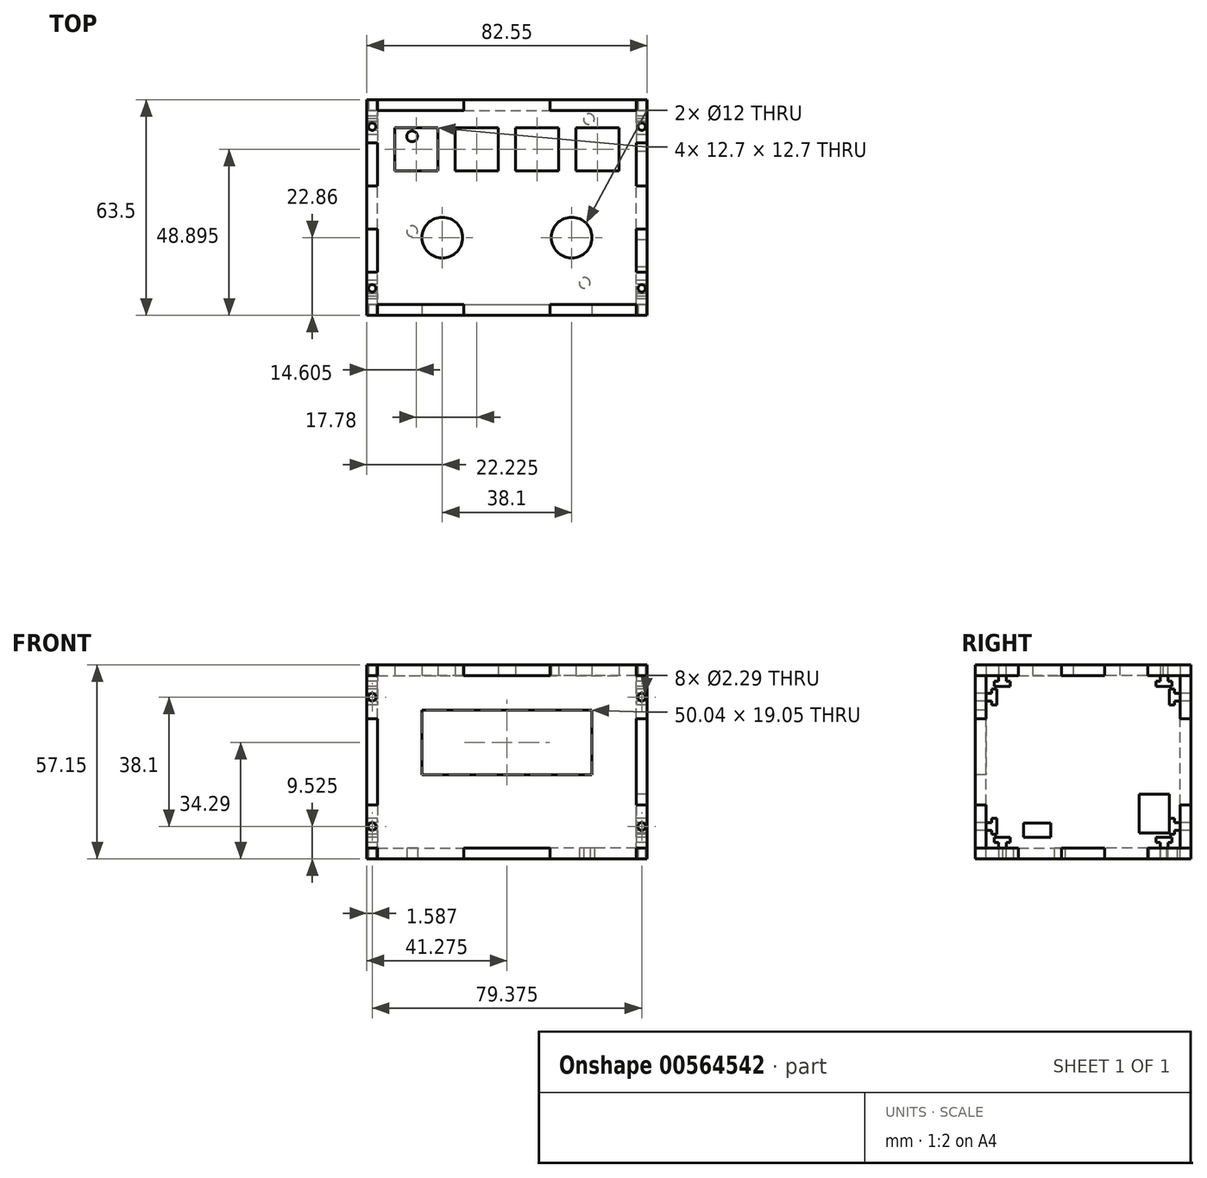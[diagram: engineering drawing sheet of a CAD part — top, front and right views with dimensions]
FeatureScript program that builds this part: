
annotation { "Feature Type Name" : "Feature", "Feature Type Description" : "" }
export const myFeature = defineFeature(function(context is Context, id is Id, definition is map)
    precondition{}
    {
        {
            var Q0;
            Q0=qCreatedBy(makeId("Top.planeOp"),FACE);
            var sketch = newSketch(context, id + "F0", { "sketchPlane" : qUnion([Q0])});
            skLineSegment(sketch, "E0.bottom", {"start": v(0, 0) * mm, "end": v(3.18, 0) * mm});
            skLineSegment(sketch, "E0.top", {"start": v(0, 63.5) * mm, "end": v(3.18, 63.5) * mm});
            skLineSegment(sketch, "E0.left", {"start": v(0, 0) * mm, "end": v(0, 12.7) * mm});
            skLineSegment(sketch, "E0.right", {"start": v(82.55, 0) * mm, "end": v(82.55, 12.7) * mm});
            skLineSegment(sketch, "E1", {"start": v(0, 12.7) * mm, "end": v(3.17, 12.7) * mm});
            skLineSegment(sketch, "E2", {"start": v(3.17, 12.7) * mm, "end": v(3.17, 25.4) * mm});
            skLineSegment(sketch, "E3", {"start": v(3.17, 25.4) * mm, "end": v(0, 25.4) * mm});
            skLineSegment(sketch, "E4.MirrorCS", {"start": v(0, 50.8) * mm, "end": v(3.17, 50.8) * mm});
            skLineSegment(sketch, "E5.MirrorCS", {"start": v(3.17, 38.1) * mm, "end": v(0, 38.1) * mm});
            skLineSegment(sketch, "E6.MirrorCS", {"start": v(3.17, 50.8) * mm, "end": v(3.17, 38.1) * mm});
            skLineSegment(sketch, "E7.MirrorCS", {"start": v(0, 63.5) * mm, "end": v(0, 50.8) * mm});
            skLineSegment(sketch, "E8.MirrorCS", {"start": v(82.55, 12.7) * mm, "end": v(79.37, 12.7) * mm});
            skLineSegment(sketch, "E9.MirrorCS", {"start": v(82.55, 50.8) * mm, "end": v(79.37, 50.8) * mm});
            skLineSegment(sketch, "E10.MirrorCS", {"start": v(79.37, 38.1) * mm, "end": v(82.55, 38.1) * mm});
            skLineSegment(sketch, "E11.MirrorCS", {"start": v(79.37, 25.4) * mm, "end": v(82.55, 25.4) * mm});
            skLineSegment(sketch, "E12.MirrorCS", {"start": v(79.37, 12.7) * mm, "end": v(79.37, 25.4) * mm});
            skLineSegment(sketch, "E13.MirrorCS", {"start": v(79.37, 50.8) * mm, "end": v(79.37, 38.1) * mm});
            skLineSegment(sketch, "E14.trimOffspring", {"start": v(0, 50.8) * mm, "end": v(0, 63.5) * mm});
            skLineSegment(sketch, "E15.trimOffspring", {"start": v(0, 25.4) * mm, "end": v(0, 38.1) * mm});
            skPoint(sketch, "E16.end.orphan", {"position": v(2.08, 31.75) * mm});
            skPoint(sketch, "E16.start.orphan", {"position": v(0, 31.75) * mm});
            skLineSegment(sketch, "E17.trimOffspring", {"start": v(0, 38.1) * mm, "end": v(0, 25.4) * mm});
            skLineSegment(sketch, "E18.trimOffspring", {"start": v(0, 12.7) * mm, "end": v(0, 0) * mm});
            skLineSegment(sketch, "E19.trimOffspring", {"start": v(82.55, 50.8) * mm, "end": v(82.55, 63.5) * mm});
            skLineSegment(sketch, "E20.trimOffspring", {"start": v(82.55, 25.4) * mm, "end": v(82.55, 38.1) * mm});
            skPoint(sketch, "E21.MirrorCS.end.orphan", {"position": v(80.47, 31.75) * mm});
            skPoint(sketch, "E21.MirrorCS.start.orphan", {"position": v(82.55, 31.75) * mm});
            skLineSegment(sketch, "E22", {"start": v(3.18, 0) * mm, "end": v(3.18, 3.17) * mm});
            skLineSegment(sketch, "E23", {"start": v(3.18, 3.17) * mm, "end": v(28.58, 3.17) * mm});
            skLineSegment(sketch, "E24", {"start": v(28.58, 3.17) * mm, "end": v(28.58, 0) * mm});
            skLineSegment(sketch, "E25.MirrorCS", {"start": v(79.37, 0) * mm, "end": v(79.37, 3.17) * mm});
            skLineSegment(sketch, "E26.MirrorCS", {"start": v(79.37, 0) * mm, "end": v(79.37, 0) * mm});
            skLineSegment(sketch, "E27.MirrorCS", {"start": v(53.97, 3.17) * mm, "end": v(53.97, 0) * mm});
            skLineSegment(sketch, "E28.MirrorCS", {"start": v(53.97, 0) * mm, "end": v(28.58, 0) * mm});
            skLineSegment(sketch, "E29.MirrorCS", {"start": v(79.37, 3.17) * mm, "end": v(53.97, 3.17) * mm});
            skLineSegment(sketch, "E30.MirrorCS", {"start": v(79.37, 63.5) * mm, "end": v(79.37, 63.5) * mm});
            skLineSegment(sketch, "E31.MirrorCS", {"start": v(3.18, 63.5) * mm, "end": v(3.18, 60.33) * mm});
            skLineSegment(sketch, "E32.MirrorCS", {"start": v(79.37, 63.5) * mm, "end": v(79.37, 60.33) * mm});
            skLineSegment(sketch, "E33.MirrorCS", {"start": v(53.97, 60.33) * mm, "end": v(53.97, 63.5) * mm});
            skLineSegment(sketch, "E34.MirrorCS", {"start": v(28.58, 60.33) * mm, "end": v(28.58, 63.5) * mm});
            skLineSegment(sketch, "E35.MirrorCS", {"start": v(79.37, 60.33) * mm, "end": v(53.97, 60.33) * mm});
            skLineSegment(sketch, "E36.MirrorCS", {"start": v(3.18, 60.33) * mm, "end": v(28.58, 60.33) * mm});
            skLineSegment(sketch, "E37.trimOffspring", {"start": v(28.58, 63.5) * mm, "end": v(53.97, 63.5) * mm});
            skLineSegment(sketch, "E38.trimOffspring", {"start": v(79.37, 63.5) * mm, "end": v(82.55, 63.5) * mm});
            skPoint(sketch, "E39.start.orphan", {"position": v(41.27, 63.5) * mm});
            skLineSegment(sketch, "E40.trimOffspring", {"start": v(3.17, 0) * mm, "end": v(0, 0) * mm});
            skLineSegment(sketch, "E41.trimOffspring", {"start": v(79.37, 0) * mm, "end": v(82.55, 0) * mm});
            skLineSegment(sketch, "E42.trimOffspring", {"start": v(28.58, 0) * mm, "end": v(53.97, 0) * mm});
            skLineSegment(sketch, "E43", {"start": v(79.37, 60.33) * mm, "end": v(65.4, 60.33) * mm});
            skLineSegment(sketch, "E44", {"start": v(79.37, 3.17) * mm, "end": v(64.13, 3.17) * mm});
            skCircle(sketch, "E45", {"center": v(65.4, 57.78) * mm, "radius": 1.59 * mm});
            skCircle(sketch, "E46", {"center": v(64.13, 9.52) * mm, "radius": 1.59 * mm});
            skCircle(sketch, "E47", {"center": v(13.33, 52.7) * mm, "radius": 1.59 * mm});
            skCircle(sketch, "E48", {"center": v(13.33, 24.76) * mm, "radius": 1.59 * mm});
            skLineSegment(sketch, "E49.trimOffspring", {"start": v(28.58, 60.33) * mm, "end": v(13.33, 60.33) * mm});
            skLineSegment(sketch, "E50.trimOffspring", {"start": v(28.58, 60.33) * mm, "end": v(14.3, 60.33) * mm});
            skPoint(sketch, "E51.start.orphan", {"position": v(64.13, 57.78) * mm});
            skLineSegment(sketch, "E52", {"start": v(82.55, 0) * mm, "end": v(82.55, 7.94) * mm});
            skLineSegment(sketch, "E53", {"start": v(82.55, 0) * mm, "end": v(80.96, 0) * mm});
            skCircle(sketch, "E54", {"center": v(1.59, 7.94) * mm, "radius": 1.09 * mm});
            skPoint(sketch, "E55.endSnap0", {"position": v(41.28, 63.5) * mm});
            skCircle(sketch, "E56.MirrorC", {"center": v(1.59, 55.56) * mm, "radius": 1.09 * mm});
            skCircle(sketch, "E57.MirrorC", {"center": v(80.96, 55.56) * mm, "radius": 1.09 * mm});
            skCircle(sketch, "E58.MirrorC", {"center": v(80.96, 7.94) * mm, "radius": 1.09 * mm});
            skPoint(sketch, "E59.MirrorCS.start.orphan", {"position": v(0, 55.56) * mm});
            skPoint(sketch, "E60.start.orphan", {"position": v(0, 7.94) * mm});
            skPoint(sketch, "E55.end.orphan", {"position": v(41.28, 60.47) * mm});
            skPoint(sketch, "E55.start.orphan", {"position": v(41.28, 63.5) * mm});
            skSolve(sketch);
        }
        {
            var Q0;
            Q0=makeQuery(id+"F0.imprint","IMPRINT",FACE,{"disambiguationData":[TD([[makeQuery(id+"F0.imprint","IMPRINT",EDGE,{"derivedFrom":sQuery(id+"F0.wireOp",EDGE,"E0.top")}),-1.0]])]});
            extrude(context, id + "F1", {"entities" : qUnion([Q0]), "depth" : 3.17 * mm, "offsetDistance" : 25.4 * mm});
        }
        {
            var Q0;
            Q0=qCreatedBy(makeId("Right.planeOp"),FACE);
            var sketch = newSketch(context, id + "F2", { "sketchPlane" : qUnion([Q0])});
            skLineSegment(sketch, "E61.top", {"start": v(12.7, 57.15) * mm, "end": v(25.4, 57.15) * mm});
            skLineSegment(sketch, "E62", {"start": v(3.18, 3.18) * mm, "end": v(6.8, 3.18) * mm});
            skLineSegment(sketch, "E63", {"start": v(12.7, 3.18) * mm, "end": v(12.7, 0) * mm});
            skLineSegment(sketch, "E64", {"start": v(12.7, 0) * mm, "end": v(25.4, 0) * mm});
            skLineSegment(sketch, "E65", {"start": v(25.4, 0) * mm, "end": v(25.4, 3.18) * mm});
            skLineSegment(sketch, "E66", {"start": v(25.4, 3.18) * mm, "end": v(38.1, 3.18) * mm});
            skLineSegment(sketch, "E67.MirrorCS", {"start": v(38.1, 0) * mm, "end": v(38.1, 3.18) * mm});
            skLineSegment(sketch, "E68.MirrorCS", {"start": v(50.8, 3.18) * mm, "end": v(50.8, 0) * mm});
            skLineSegment(sketch, "E69.MirrorCS", {"start": v(50.8, 0) * mm, "end": v(38.1, 0) * mm});
            skLineSegment(sketch, "E70.MirrorCS", {"start": v(38.1, 3.18) * mm, "end": v(25.4, 3.18) * mm});
            skLineSegment(sketch, "E71.MirrorCS", {"start": v(50.8, 53.98) * mm, "end": v(50.8, 57.15) * mm});
            skLineSegment(sketch, "E72.MirrorCS", {"start": v(38.1, 57.15) * mm, "end": v(38.1, 53.98) * mm});
            skLineSegment(sketch, "E73.MirrorCS", {"start": v(12.7, 53.98) * mm, "end": v(12.7, 57.15) * mm});
            skLineSegment(sketch, "E74.MirrorCS", {"start": v(25.4, 57.15) * mm, "end": v(25.4, 53.98) * mm});
            skLineSegment(sketch, "E75.MirrorCS", {"start": v(25.4, 53.98) * mm, "end": v(38.1, 53.98) * mm});
            skLineSegment(sketch, "E76.MirrorCS", {"start": v(38.1, 53.98) * mm, "end": v(25.4, 53.98) * mm});
            skLineSegment(sketch, "E77.MirrorCS", {"start": v(50.8, 57.15) * mm, "end": v(38.1, 57.15) * mm});
            skLineSegment(sketch, "E78.MirrorCS", {"start": v(60.32, 53.98) * mm, "end": v(56.7, 53.98) * mm});
            skLineSegment(sketch, "E79.MirrorCS", {"start": v(3.18, 53.98) * mm, "end": v(6.8, 53.98) * mm});
            skLineSegment(sketch, "E80.trimOffspring", {"start": v(38.1, 57.15) * mm, "end": v(50.8, 57.15) * mm});
            skPoint(sketch, "E81.orphan", {"position": v(31.75, 57.15) * mm});
            skPoint(sketch, "E82.MirrorCS.start.orphan", {"position": v(63.5, 57.15) * mm});
            skLineSegment(sketch, "E83.trimOffspring", {"start": v(38.1, 0) * mm, "end": v(50.8, 0) * mm});
            skPoint(sketch, "E84.MirrorCS.start.orphan", {"position": v(63.5, 0) * mm});
            skPoint(sketch, "E85.orphan", {"position": v(0, 57.15) * mm});
            skLineSegment(sketch, "E86", {"start": v(0, 15.87) * mm, "end": v(3.18, 15.87) * mm});
            skLineSegment(sketch, "E87", {"start": v(3.18, 15.87) * mm, "end": v(3.18, 10.67) * mm});
            skLineSegment(sketch, "E88.trimOffspring", {"start": v(0, 15.87) * mm, "end": v(0, 41.28) * mm});
            skLineSegment(sketch, "E89.MirrorCS", {"start": v(3.18, 41.28) * mm, "end": v(3.18, 46.48) * mm});
            skLineSegment(sketch, "E90.MirrorCS", {"start": v(0, 41.28) * mm, "end": v(0, 15.87) * mm});
            skLineSegment(sketch, "E91.MirrorCS", {"start": v(0, 41.28) * mm, "end": v(3.18, 41.28) * mm});
            skLineSegment(sketch, "E92.MirrorCS", {"start": v(63.5, 41.28) * mm, "end": v(60.32, 41.28) * mm});
            skLineSegment(sketch, "E93.MirrorCS", {"start": v(63.5, 15.87) * mm, "end": v(60.32, 15.87) * mm});
            skLineSegment(sketch, "E94.MirrorCS", {"start": v(60.32, 41.28) * mm, "end": v(60.32, 46.48) * mm});
            skLineSegment(sketch, "E95.MirrorCS", {"start": v(63.5, 15.87) * mm, "end": v(63.5, 41.28) * mm});
            skLineSegment(sketch, "E96.MirrorCS", {"start": v(60.32, 15.87) * mm, "end": v(60.32, 10.67) * mm});
            skLineSegment(sketch, "E97.MirrorCS", {"start": v(63.5, 41.28) * mm, "end": v(63.5, 15.87) * mm});
            skPoint(sketch, "E98.MirrorCS.end.orphan", {"position": v(58.61, 28.58) * mm});
            skPoint(sketch, "E98.MirrorCS.start.orphan", {"position": v(63.5, 28.58) * mm});
            skPoint(sketch, "E99.orphan", {"position": v(63.5, 3.17) * mm});
            skPoint(sketch, "E100.orphan", {"position": v(0, 3.17) * mm});
            skPoint(sketch, "E101.end.orphan", {"position": v(4.89, 28.58) * mm});
            skPoint(sketch, "E101.start.orphan", {"position": v(0, 28.58) * mm});
            skPoint(sketch, "E61.left.start.orphan", {"position": v(0, 0) * mm});
            skLineSegment(sketch, "E102.top", {"start": v(56.7, 6.35) * mm, "end": v(54.42, 6.35) * mm});
            skLineSegment(sketch, "E102.left", {"start": v(56.7, 3.18) * mm, "end": v(56.7, 4.83) * mm});
            skLineSegment(sketch, "E102.right", {"start": v(54.42, 3.18) * mm, "end": v(54.42, 4.83) * mm});
            skPoint(sketch, "E103.end.orphan", {"position": v(54.42, 3.18) * mm});
            skLineSegment(sketch, "E104.trimOffspring", {"start": v(54.42, 3.18) * mm, "end": v(50.8, 3.18) * mm});
            skPoint(sketch, "E105.start.orphan", {"position": v(55.56, 3.18) * mm});
            skLineSegment(sketch, "E106", {"start": v(56.7, 3.18) * mm, "end": v(60.32, 3.18) * mm});
            skLineSegment(sketch, "E107.bottom", {"start": v(57.91, 6.35) * mm, "end": v(53.21, 6.35) * mm});
            skLineSegment(sketch, "E107.top", {"start": v(57.91, 4.83) * mm, "end": v(56.7, 4.83) * mm});
            skLineSegment(sketch, "E107.left", {"start": v(57.91, 6.35) * mm, "end": v(57.91, 4.83) * mm});
            skLineSegment(sketch, "E107.right", {"start": v(53.21, 6.35) * mm, "end": v(53.21, 4.83) * mm});
            skPoint(sketch, "E107.middle", {"position": v(55.56, 5.59) * mm});
            skLineSegment(sketch, "E108.trimOffspring", {"start": v(54.42, 4.83) * mm, "end": v(53.21, 4.83) * mm});
            skPoint(sketch, "E109.start.orphan", {"position": v(55.56, 6.35) * mm});
            skLineSegment(sketch, "E110.MirrorCS", {"start": v(54.42, 52.32) * mm, "end": v(53.21, 52.32) * mm});
            skLineSegment(sketch, "E111.MirrorCS", {"start": v(57.91, 52.32) * mm, "end": v(56.7, 52.32) * mm});
            skLineSegment(sketch, "E112.MirrorCS", {"start": v(56.7, 53.98) * mm, "end": v(56.7, 52.32) * mm});
            skLineSegment(sketch, "E113.MirrorCS", {"start": v(54.42, 53.98) * mm, "end": v(54.42, 52.32) * mm});
            skLineSegment(sketch, "E114.MirrorCS", {"start": v(56.7, 50.8) * mm, "end": v(54.42, 50.8) * mm});
            skLineSegment(sketch, "E115.MirrorCS", {"start": v(53.21, 50.8) * mm, "end": v(53.21, 52.32) * mm});
            skPoint(sketch, "E116.MirrorP", {"position": v(54.42, 53.98) * mm});
            skPoint(sketch, "E117.MirrorP", {"position": v(55.56, 50.8) * mm});
            skLineSegment(sketch, "E118.MirrorCS", {"start": v(57.91, 50.8) * mm, "end": v(53.21, 50.8) * mm});
            skLineSegment(sketch, "E119.MirrorCS", {"start": v(57.91, 50.8) * mm, "end": v(57.91, 52.32) * mm});
            skPoint(sketch, "E120.MirrorP", {"position": v(55.56, 53.98) * mm});
            skPoint(sketch, "E121.MirrorP", {"position": v(55.56, 51.56) * mm});
            skLineSegment(sketch, "E122.MirrorCS", {"start": v(6.8, 6.35) * mm, "end": v(9.08, 6.35) * mm});
            skLineSegment(sketch, "E123.MirrorCS", {"start": v(9.08, 4.83) * mm, "end": v(10.29, 4.83) * mm});
            skLineSegment(sketch, "E124.MirrorCS", {"start": v(9.08, 3.18) * mm, "end": v(9.08, 4.83) * mm});
            skLineSegment(sketch, "E125.MirrorCS", {"start": v(6.8, 3.18) * mm, "end": v(6.8, 4.83) * mm});
            skLineSegment(sketch, "E126.MirrorCS", {"start": v(5.59, 4.83) * mm, "end": v(6.8, 4.83) * mm});
            skLineSegment(sketch, "E127.MirrorCS", {"start": v(6.8, 3.18) * mm, "end": v(3.17, 3.18) * mm});
            skPoint(sketch, "E128.MirrorP", {"position": v(7.94, 6.35) * mm});
            skLineSegment(sketch, "E129.MirrorCS", {"start": v(9.08, 3.18) * mm, "end": v(12.7, 3.18) * mm});
            skLineSegment(sketch, "E130.MirrorCS", {"start": v(5.59, 6.35) * mm, "end": v(10.29, 6.35) * mm});
            skPoint(sketch, "E131.MirrorP", {"position": v(9.08, 3.18) * mm});
            skPoint(sketch, "E132.MirrorP", {"position": v(7.94, 5.59) * mm});
            skLineSegment(sketch, "E133.MirrorCS", {"start": v(5.59, 6.35) * mm, "end": v(5.59, 4.83) * mm});
            skLineSegment(sketch, "E134.MirrorCS", {"start": v(10.29, 6.35) * mm, "end": v(10.29, 4.83) * mm});
            skPoint(sketch, "E135.MirrorP", {"position": v(7.94, 3.18) * mm});
            skLineSegment(sketch, "E136.MirrorCS", {"start": v(6.8, 50.8) * mm, "end": v(9.08, 50.8) * mm});
            skLineSegment(sketch, "E137.MirrorCS", {"start": v(10.29, 50.8) * mm, "end": v(10.29, 52.32) * mm});
            skLineSegment(sketch, "E138.MirrorCS", {"start": v(9.08, 52.32) * mm, "end": v(10.29, 52.32) * mm});
            skLineSegment(sketch, "E139.MirrorCS", {"start": v(6.8, 53.98) * mm, "end": v(6.8, 52.32) * mm});
            skPoint(sketch, "E140.MirrorP", {"position": v(7.94, 51.56) * mm});
            skLineSegment(sketch, "E141.MirrorCS", {"start": v(5.59, 50.8) * mm, "end": v(10.29, 50.8) * mm});
            skLineSegment(sketch, "E142.MirrorCS", {"start": v(5.59, 50.8) * mm, "end": v(5.59, 52.32) * mm});
            skLineSegment(sketch, "E143.MirrorCS", {"start": v(5.59, 52.32) * mm, "end": v(6.8, 52.32) * mm});
            skPoint(sketch, "E144.MirrorP", {"position": v(9.08, 53.98) * mm});
            skPoint(sketch, "E145.MirrorP", {"position": v(7.94, 50.8) * mm});
            skPoint(sketch, "E146.MirrorP", {"position": v(7.94, 53.98) * mm});
            skLineSegment(sketch, "E147.MirrorCS", {"start": v(9.08, 53.98) * mm, "end": v(9.08, 52.32) * mm});
            skLineSegment(sketch, "E148.trimOffspring", {"start": v(54.42, 53.98) * mm, "end": v(50.8, 53.98) * mm});
            skLineSegment(sketch, "E149.trimOffspring", {"start": v(9.08, 53.98) * mm, "end": v(12.7, 53.98) * mm});
            skPoint(sketch, "E150.MirrorCS.start.orphan", {"position": v(3.17, 53.98) * mm});
            skLineSegment(sketch, "E151.bottom", {"start": v(60.32, 10.67) * mm, "end": v(58.67, 10.67) * mm});
            skLineSegment(sketch, "E151.top", {"start": v(60.32, 8.38) * mm, "end": v(58.67, 8.38) * mm});
            skLineSegment(sketch, "E151.right", {"start": v(57.15, 10.67) * mm, "end": v(57.15, 8.38) * mm});
            skLineSegment(sketch, "E152.bottom", {"start": v(57.15, 7.18) * mm, "end": v(58.67, 7.18) * mm});
            skLineSegment(sketch, "E152.top", {"start": v(57.15, 11.87) * mm, "end": v(58.67, 11.87) * mm});
            skLineSegment(sketch, "E152.left", {"start": v(57.15, 7.18) * mm, "end": v(57.15, 11.87) * mm});
            skLineSegment(sketch, "E152.right", {"start": v(58.67, 7.18) * mm, "end": v(58.67, 8.38) * mm});
            skPoint(sketch, "E152.middle", {"position": v(57.91, 9.52) * mm});
            skLineSegment(sketch, "E153.trimOffspring", {"start": v(58.67, 10.67) * mm, "end": v(58.67, 11.87) * mm});
            skPoint(sketch, "E154.start.orphan", {"position": v(57.15, 9.53) * mm});
            skLineSegment(sketch, "E155.trimOffspring", {"start": v(60.32, 8.38) * mm, "end": v(60.32, 3.18) * mm});
            skPoint(sketch, "E156.orphan", {"position": v(60.32, 8.38) * mm});
            skPoint(sketch, "E151.left.end.orphan", {"position": v(60.32, 9.52) * mm});
            skPoint(sketch, "E157.MirrorP", {"position": v(57.91, 47.63) * mm});
            skPoint(sketch, "E158.MirrorP", {"position": v(57.15, 47.63) * mm});
            skLineSegment(sketch, "E159.MirrorCS", {"start": v(57.15, 46.48) * mm, "end": v(57.15, 48.77) * mm});
            skLineSegment(sketch, "E160.MirrorCS", {"start": v(57.15, 45.28) * mm, "end": v(58.67, 45.28) * mm});
            skLineSegment(sketch, "E161.MirrorCS", {"start": v(57.15, 49.97) * mm, "end": v(57.15, 45.28) * mm});
            skLineSegment(sketch, "E162.MirrorCS", {"start": v(60.32, 48.77) * mm, "end": v(58.67, 48.77) * mm});
            skLineSegment(sketch, "E163.MirrorCS", {"start": v(57.15, 49.97) * mm, "end": v(58.67, 49.97) * mm});
            skLineSegment(sketch, "E164.MirrorCS", {"start": v(60.32, 46.48) * mm, "end": v(58.67, 46.48) * mm});
            skLineSegment(sketch, "E165.MirrorCS", {"start": v(58.67, 49.97) * mm, "end": v(58.67, 48.77) * mm});
            skLineSegment(sketch, "E166.MirrorCS", {"start": v(58.67, 46.48) * mm, "end": v(58.67, 45.28) * mm});
            skLineSegment(sketch, "E167.MirrorCS", {"start": v(6.35, 46.48) * mm, "end": v(6.35, 48.77) * mm});
            skLineSegment(sketch, "E168.MirrorCS", {"start": v(3.17, 41.28) * mm, "end": v(3.17, 46.48) * mm});
            skLineSegment(sketch, "E169.MirrorCS", {"start": v(6.35, 49.97) * mm, "end": v(4.83, 49.97) * mm});
            skLineSegment(sketch, "E170.MirrorCS", {"start": v(6.35, 49.97) * mm, "end": v(6.35, 45.28) * mm});
            skPoint(sketch, "E171.MirrorP", {"position": v(5.59, 47.63) * mm});
            skLineSegment(sketch, "E172.MirrorCS", {"start": v(4.83, 46.48) * mm, "end": v(4.83, 45.28) * mm});
            skLineSegment(sketch, "E173.MirrorCS", {"start": v(3.17, 46.48) * mm, "end": v(4.83, 46.48) * mm});
            skLineSegment(sketch, "E174.MirrorCS", {"start": v(4.83, 49.97) * mm, "end": v(4.83, 48.77) * mm});
            skLineSegment(sketch, "E175.MirrorCS", {"start": v(3.17, 48.77) * mm, "end": v(4.83, 48.77) * mm});
            skLineSegment(sketch, "E176.MirrorCS", {"start": v(6.35, 45.28) * mm, "end": v(4.83, 45.28) * mm});
            skPoint(sketch, "E177.MirrorP", {"position": v(6.35, 47.63) * mm});
            skPoint(sketch, "E178.MirrorP", {"position": v(5.59, 9.52) * mm});
            skPoint(sketch, "E179.MirrorP", {"position": v(6.35, 9.52) * mm});
            skLineSegment(sketch, "E180.MirrorCS", {"start": v(6.35, 10.67) * mm, "end": v(6.35, 8.38) * mm});
            skLineSegment(sketch, "E181.MirrorCS", {"start": v(3.17, 8.38) * mm, "end": v(4.83, 8.38) * mm});
            skLineSegment(sketch, "E182.MirrorCS", {"start": v(6.35, 7.18) * mm, "end": v(6.35, 11.87) * mm});
            skLineSegment(sketch, "E183.MirrorCS", {"start": v(4.83, 10.67) * mm, "end": v(4.83, 11.87) * mm});
            skPoint(sketch, "E184.MirrorP", {"position": v(3.17, 9.52) * mm});
            skLineSegment(sketch, "E185.MirrorCS", {"start": v(3.17, 8.38) * mm, "end": v(3.17, 3.18) * mm});
            skLineSegment(sketch, "E186.MirrorCS", {"start": v(3.17, 10.67) * mm, "end": v(4.83, 10.67) * mm});
            skLineSegment(sketch, "E187.MirrorCS", {"start": v(4.83, 7.18) * mm, "end": v(4.83, 8.38) * mm});
            skLineSegment(sketch, "E188.MirrorCS", {"start": v(3.17, 15.87) * mm, "end": v(3.17, 10.67) * mm});
            skLineSegment(sketch, "E189.MirrorCS", {"start": v(6.35, 7.18) * mm, "end": v(4.83, 7.18) * mm});
            skLineSegment(sketch, "E190.MirrorCS", {"start": v(6.35, 11.87) * mm, "end": v(4.83, 11.87) * mm});
            skPoint(sketch, "E191.MirrorP", {"position": v(3.17, 8.38) * mm});
            skLineSegment(sketch, "E192.trimOffspring", {"start": v(60.32, 48.77) * mm, "end": v(60.32, 53.98) * mm});
            skLineSegment(sketch, "E193.trimOffspring", {"start": v(3.17, 48.77) * mm, "end": v(3.17, 53.98) * mm});
            skLineSegment(sketch, "E194.trimOffspring", {"start": v(3.18, 8.38) * mm, "end": v(3.18, 3.18) * mm});
            skLineSegment(sketch, "E195.trimOffspring", {"start": v(3.18, 48.77) * mm, "end": v(3.18, 53.98) * mm});
            skPoint(sketch, "E196.start.orphan", {"position": v(31.75, 3.18) * mm});
            skSolve(sketch);
        }
        {
            var Q0;
            Q0 = qSketchRegion(id + "F2", true);
            extrude(context, id + "F3", {"entities" : qUnion([Q0]), "depth" : 3.17 * mm, "offsetDistance" : 25.4 * mm});
        }
        {
            var Q0;
            Q0=qCreatedBy(makeId("Front.planeOp"),FACE);
            var sketch = newSketch(context, id + "F4", { "sketchPlane" : qUnion([Q0])});
            skLineSegment(sketch, "E197.bottom", {"start": v(3.17, 0) * mm, "end": v(28.58, 0) * mm});
            skLineSegment(sketch, "E197.top", {"start": v(3.17, 57.15) * mm, "end": v(28.58, 57.15) * mm});
            skLineSegment(sketch, "E198.top", {"start": v(0, 3.18) * mm, "end": v(3.17, 3.18) * mm});
            skLineSegment(sketch, "E198.right", {"start": v(3.18, 0) * mm, "end": v(3.17, 3.18) * mm});
            skLineSegment(sketch, "E199", {"start": v(3.18, 0) * mm, "end": v(28.58, 0) * mm});
            skLineSegment(sketch, "E200.top", {"start": v(28.58, 3.18) * mm, "end": v(53.98, 3.18) * mm});
            skLineSegment(sketch, "E200.left", {"start": v(28.58, 0) * mm, "end": v(28.58, 3.18) * mm});
            skLineSegment(sketch, "E200.right", {"start": v(53.98, 0) * mm, "end": v(53.98, 3.18) * mm});
            skPoint(sketch, "E201.endSnap0", {"position": v(41.28, 3.18) * mm});
            skLineSegment(sketch, "E202.MirrorCS", {"start": v(82.55, 3.18) * mm, "end": v(79.38, 3.17) * mm});
            skLineSegment(sketch, "E203.MirrorCS", {"start": v(79.38, 0) * mm, "end": v(79.38, 3.18) * mm});
            skLineSegment(sketch, "E204.MirrorCS", {"start": v(82.55, 53.98) * mm, "end": v(79.38, 53.98) * mm});
            skLineSegment(sketch, "E205.MirrorCS", {"start": v(53.98, 57.15) * mm, "end": v(53.98, 53.98) * mm});
            skLineSegment(sketch, "E206.MirrorCS", {"start": v(28.58, 57.15) * mm, "end": v(28.58, 53.98) * mm});
            skLineSegment(sketch, "E207.MirrorCS", {"start": v(0, 53.98) * mm, "end": v(3.17, 53.98) * mm});
            skLineSegment(sketch, "E208.MirrorCS", {"start": v(3.18, 57.15) * mm, "end": v(3.17, 53.98) * mm});
            skLineSegment(sketch, "E209.MirrorCS", {"start": v(79.38, 57.15) * mm, "end": v(79.38, 53.98) * mm});
            skLineSegment(sketch, "E210.MirrorCS", {"start": v(28.58, 53.98) * mm, "end": v(53.98, 53.98) * mm});
            skLineSegment(sketch, "E211.MirrorCS", {"start": v(3.18, 57.15) * mm, "end": v(28.58, 57.15) * mm});
            skPoint(sketch, "E212.MirrorP", {"position": v(41.28, 53.98) * mm});
            skPoint(sketch, "E213.orphan", {"position": v(0, 57.15) * mm});
            skPoint(sketch, "E214.orphan", {"position": v(82.55, 57.15) * mm});
            skPoint(sketch, "E215.start.orphan", {"position": v(0, 28.58) * mm});
            skPoint(sketch, "E216.MirrorCS.start.orphan", {"position": v(82.55, 0) * mm});
            skLineSegment(sketch, "E217.trimOffspring", {"start": v(53.98, 57.15) * mm, "end": v(79.38, 57.15) * mm});
            skLineSegment(sketch, "E218", {"start": v(53.98, 0) * mm, "end": v(79.38, 0) * mm});
            skLineSegment(sketch, "E219", {"start": v(0, 3.18) * mm, "end": v(0, 15.88) * mm});
            skLineSegment(sketch, "E220.bottom", {"start": v(0, 15.88) * mm, "end": v(3.18, 15.88) * mm});
            skLineSegment(sketch, "E220.top", {"start": v(0, 41.28) * mm, "end": v(3.17, 41.28) * mm});
            skLineSegment(sketch, "E220.right", {"start": v(3.18, 15.88) * mm, "end": v(3.17, 41.28) * mm});
            skLineSegment(sketch, "E221.trimOffspring", {"start": v(0, 41.28) * mm, "end": v(0, 53.98) * mm});
            skLineSegment(sketch, "E222.MirrorCS", {"start": v(82.55, 41.28) * mm, "end": v(82.55, 53.98) * mm});
            skLineSegment(sketch, "E223.MirrorCS", {"start": v(79.38, 57.15) * mm, "end": v(53.98, 57.15) * mm});
            skLineSegment(sketch, "E224.MirrorCS", {"start": v(82.55, 3.18) * mm, "end": v(79.38, 3.18) * mm});
            skLineSegment(sketch, "E225.MirrorCS", {"start": v(82.55, 15.88) * mm, "end": v(79.38, 15.88) * mm});
            skLineSegment(sketch, "E226.MirrorCS", {"start": v(82.55, 41.28) * mm, "end": v(79.38, 41.28) * mm});
            skLineSegment(sketch, "E227.MirrorCS", {"start": v(79.38, 0) * mm, "end": v(53.98, 0) * mm});
            skLineSegment(sketch, "E228.MirrorCS", {"start": v(82.55, 3.18) * mm, "end": v(82.55, 15.88) * mm});
            skPoint(sketch, "E229.MirrorP", {"position": v(82.55, 28.58) * mm});
            skLineSegment(sketch, "E230.MirrorCS", {"start": v(79.38, 15.88) * mm, "end": v(79.38, 41.28) * mm});
            skPoint(sketch, "E231.orphan", {"position": v(28.58, 0) * mm});
            skPoint(sketch, "E201.end.orphan", {"position": v(41.28, 6.6) * mm});
            skPoint(sketch, "E201.start.orphan", {"position": v(41.28, 3.18) * mm});
            skPoint(sketch, "E232.orphan", {"position": v(0, 0) * mm});
            skLineSegment(sketch, "E233.bottom", {"start": v(16.26, 43.82) * mm, "end": v(66.3, 43.82) * mm});
            skLineSegment(sketch, "E233.top", {"start": v(16.26, 24.77) * mm, "end": v(66.3, 24.77) * mm});
            skLineSegment(sketch, "E233.left", {"start": v(16.26, 43.82) * mm, "end": v(16.26, 24.77) * mm});
            skLineSegment(sketch, "E233.right", {"start": v(66.3, 43.82) * mm, "end": v(66.3, 24.77) * mm});
            skPoint(sketch, "E233.middle", {"position": v(41.28, 34.3) * mm});
            skLineSegment(sketch, "E234", {"start": v(0, 0) * mm, "end": v(0, 9.53) * mm});
            skCircle(sketch, "E235", {"center": v(1.59, 9.52) * mm, "radius": 1.14 * mm});
            skPoint(sketch, "E235.centerSnap0", {"position": v(1.59, 3.18) * mm});
            skPoint(sketch, "E236.endSnap0", {"position": v(3.17, 28.58) * mm});
            skPoint(sketch, "E237.endSnap0", {"position": v(41.27, 53.98) * mm});
            skCircle(sketch, "E238.MirrorC", {"center": v(1.59, 47.63) * mm, "radius": 1.14 * mm});
            skCircle(sketch, "E239.MirrorC", {"center": v(80.96, 47.63) * mm, "radius": 1.14 * mm});
            skCircle(sketch, "E240.MirrorC", {"center": v(80.96, 9.52) * mm, "radius": 1.14 * mm});
            skPoint(sketch, "E236.end.orphan", {"position": v(1.54, 28.58) * mm});
            skPoint(sketch, "E236.start.orphan", {"position": v(3.17, 28.58) * mm});
            skPoint(sketch, "E237.end.orphan", {"position": v(41.27, 55.6) * mm});
            skPoint(sketch, "E237.start.orphan", {"position": v(41.27, 53.98) * mm});
            skPoint(sketch, "E241.end.orphan", {"position": v(0, 9.52) * mm});
            skSolve(sketch);
        }
        {
            var Q0;
            Q0=makeQuery(id+"F4.imprint","IMPRINT",FACE,{"disambiguationData":[TD([[makeQuery(id+"F4.imprint","IMPRINT",EDGE,{"derivedFrom":sQuery(id+"F4.wireOp",EDGE,"E198.top")}),1.0]])]});
            extrude(context, id + "F5", {"entities" : qUnion([Q0]), "oppositeDirection" : true, "depth" : 3.17 * mm, "offsetDistance" : 25.4 * mm});
        }
        {
            var Q0;
            Q0=qCreatedBy(makeId("Top.planeOp"),FACE);
            var sketch = newSketch(context, id + "F6", { "sketchPlane" : qUnion([Q0])});
            skLineSegment(sketch, "E242.bottom", {"start": v(0, 0) * mm, "end": v(3.18, 0) * mm});
            skLineSegment(sketch, "E242.top", {"start": v(0, 63.5) * mm, "end": v(3.18, 63.5) * mm});
            skLineSegment(sketch, "E242.left", {"start": v(0, 0) * mm, "end": v(0, 12.7) * mm});
            skLineSegment(sketch, "E242.right", {"start": v(82.55, 0) * mm, "end": v(82.55, 12.7) * mm});
            skLineSegment(sketch, "E243", {"start": v(0, 12.7) * mm, "end": v(3.18, 12.7) * mm});
            skLineSegment(sketch, "E244", {"start": v(3.18, 12.7) * mm, "end": v(3.18, 25.4) * mm});
            skLineSegment(sketch, "E245", {"start": v(3.17, 25.4) * mm, "end": v(0, 25.4) * mm});
            skLineSegment(sketch, "E246.MirrorCS", {"start": v(0, 50.8) * mm, "end": v(3.18, 50.8) * mm});
            skLineSegment(sketch, "E247.MirrorCS", {"start": v(3.17, 38.1) * mm, "end": v(0, 38.1) * mm});
            skLineSegment(sketch, "E248.MirrorCS", {"start": v(3.18, 50.8) * mm, "end": v(3.18, 38.1) * mm});
            skLineSegment(sketch, "E249.MirrorCS", {"start": v(0, 63.5) * mm, "end": v(0, 50.8) * mm});
            skLineSegment(sketch, "E250.MirrorCS", {"start": v(82.55, 12.7) * mm, "end": v(79.37, 12.7) * mm});
            skLineSegment(sketch, "E251.MirrorCS", {"start": v(82.55, 50.8) * mm, "end": v(79.37, 50.8) * mm});
            skLineSegment(sketch, "E252.MirrorCS", {"start": v(79.37, 38.1) * mm, "end": v(82.55, 38.1) * mm});
            skLineSegment(sketch, "E253.MirrorCS", {"start": v(79.37, 25.4) * mm, "end": v(82.55, 25.4) * mm});
            skLineSegment(sketch, "E254.MirrorCS", {"start": v(79.37, 12.7) * mm, "end": v(79.37, 25.4) * mm});
            skLineSegment(sketch, "E255.MirrorCS", {"start": v(79.37, 50.8) * mm, "end": v(79.37, 38.1) * mm});
            skLineSegment(sketch, "E256.trimOffspring", {"start": v(0, 50.8) * mm, "end": v(0, 63.5) * mm});
            skLineSegment(sketch, "E257.trimOffspring", {"start": v(0, 25.4) * mm, "end": v(0, 38.1) * mm});
            skPoint(sketch, "E258.end.orphan", {"position": v(2.08, 31.75) * mm});
            skPoint(sketch, "E258.start.orphan", {"position": v(0, 31.75) * mm});
            skLineSegment(sketch, "E259.trimOffspring", {"start": v(0, 38.1) * mm, "end": v(0, 25.4) * mm});
            skLineSegment(sketch, "E260.trimOffspring", {"start": v(0, 12.7) * mm, "end": v(0, 0) * mm});
            skLineSegment(sketch, "E261.trimOffspring", {"start": v(82.55, 50.8) * mm, "end": v(82.55, 63.5) * mm});
            skLineSegment(sketch, "E262.trimOffspring", {"start": v(82.55, 25.4) * mm, "end": v(82.55, 38.1) * mm});
            skPoint(sketch, "E263.MirrorCS.end.orphan", {"position": v(80.47, 31.75) * mm});
            skPoint(sketch, "E263.MirrorCS.start.orphan", {"position": v(82.55, 31.75) * mm});
            skLineSegment(sketch, "E264", {"start": v(3.18, 0) * mm, "end": v(3.18, 3.18) * mm});
            skLineSegment(sketch, "E265", {"start": v(3.18, 3.18) * mm, "end": v(28.58, 3.18) * mm});
            skLineSegment(sketch, "E266", {"start": v(28.58, 3.17) * mm, "end": v(28.58, 0) * mm});
            skLineSegment(sketch, "E267.MirrorCS", {"start": v(79.37, 0) * mm, "end": v(79.37, 3.18) * mm});
            skLineSegment(sketch, "E268.MirrorCS", {"start": v(53.97, 3.17) * mm, "end": v(53.97, 0) * mm});
            skLineSegment(sketch, "E269.MirrorCS", {"start": v(53.97, 0) * mm, "end": v(28.58, 0) * mm});
            skLineSegment(sketch, "E270.MirrorCS", {"start": v(79.37, 3.18) * mm, "end": v(53.97, 3.18) * mm});
            skLineSegment(sketch, "E271.MirrorCS", {"start": v(3.18, 63.5) * mm, "end": v(3.18, 60.33) * mm});
            skLineSegment(sketch, "E272.MirrorCS", {"start": v(79.37, 63.5) * mm, "end": v(79.37, 60.33) * mm});
            skLineSegment(sketch, "E273.MirrorCS", {"start": v(53.97, 60.33) * mm, "end": v(53.97, 63.5) * mm});
            skLineSegment(sketch, "E274.MirrorCS", {"start": v(28.58, 60.33) * mm, "end": v(28.58, 63.5) * mm});
            skLineSegment(sketch, "E275.MirrorCS", {"start": v(79.37, 60.33) * mm, "end": v(53.97, 60.33) * mm});
            skLineSegment(sketch, "E276.MirrorCS", {"start": v(3.18, 60.33) * mm, "end": v(28.58, 60.33) * mm});
            skLineSegment(sketch, "E277.trimOffspring", {"start": v(28.58, 63.5) * mm, "end": v(53.97, 63.5) * mm});
            skLineSegment(sketch, "E278.trimOffspring", {"start": v(79.37, 63.5) * mm, "end": v(82.55, 63.5) * mm});
            skPoint(sketch, "E279.start.orphan", {"position": v(41.27, 63.5) * mm});
            skLineSegment(sketch, "E280.trimOffspring", {"start": v(3.17, 0) * mm, "end": v(0, 0) * mm});
            skLineSegment(sketch, "E281.trimOffspring", {"start": v(79.37, 0) * mm, "end": v(82.55, 0) * mm});
            skLineSegment(sketch, "E282.trimOffspring", {"start": v(28.58, 0) * mm, "end": v(53.97, 0) * mm});
            skLineSegment(sketch, "E283", {"start": v(79.37, 60.33) * mm, "end": v(65.4, 60.33) * mm});
            skLineSegment(sketch, "E284", {"start": v(79.37, 3.18) * mm, "end": v(64.13, 3.18) * mm});
            skLineSegment(sketch, "E285.trimOffspring", {"start": v(28.57, 60.33) * mm, "end": v(13.33, 60.33) * mm});
            skLineSegment(sketch, "E286.trimOffspring", {"start": v(28.57, 60.33) * mm, "end": v(14.3, 60.33) * mm});
            skLineSegment(sketch, "E287", {"start": v(3.18, 60.33) * mm, "end": v(8.26, 60.33) * mm});
            skLineSegment(sketch, "E288.bottom", {"start": v(8.26, 55.25) * mm, "end": v(20.96, 55.25) * mm});
            skLineSegment(sketch, "E288.top", {"start": v(8.26, 42.55) * mm, "end": v(20.96, 42.55) * mm});
            skLineSegment(sketch, "E288.left", {"start": v(8.26, 55.25) * mm, "end": v(8.26, 42.55) * mm});
            skLineSegment(sketch, "E288.right", {"start": v(20.96, 55.25) * mm, "end": v(20.96, 42.55) * mm});
            skLineSegment(sketch, "E289.1.0.0", {"start": v(26.04, 42.55) * mm, "end": v(38.74, 42.55) * mm});
            skLineSegment(sketch, "E289.1.0.1", {"start": v(26.04, 55.25) * mm, "end": v(38.74, 55.25) * mm});
            skLineSegment(sketch, "E289.1.0.2", {"start": v(38.74, 55.25) * mm, "end": v(38.74, 42.55) * mm});
            skLineSegment(sketch, "E289.1.0.3", {"start": v(26.04, 55.25) * mm, "end": v(26.04, 42.55) * mm});
            skLineSegment(sketch, "E289.2.0.0", {"start": v(43.82, 42.55) * mm, "end": v(56.52, 42.55) * mm});
            skLineSegment(sketch, "E289.2.0.1", {"start": v(43.82, 55.25) * mm, "end": v(56.52, 55.25) * mm});
            skLineSegment(sketch, "E289.2.0.2", {"start": v(56.52, 55.25) * mm, "end": v(56.52, 42.55) * mm});
            skLineSegment(sketch, "E289.2.0.3", {"start": v(43.82, 55.25) * mm, "end": v(43.82, 42.55) * mm});
            skLineSegment(sketch, "E289.3.0.0", {"start": v(61.6, 42.55) * mm, "end": v(74.3, 42.55) * mm});
            skLineSegment(sketch, "E289.3.0.1", {"start": v(61.6, 55.25) * mm, "end": v(74.3, 55.25) * mm});
            skLineSegment(sketch, "E289.3.0.2", {"start": v(74.3, 55.25) * mm, "end": v(74.3, 42.55) * mm});
            skLineSegment(sketch, "E289.3.0.3", {"start": v(61.6, 55.25) * mm, "end": v(61.6, 42.55) * mm});
            skPoint(sketch, "E290.end.orphan", {"position": v(3.18, 55.25) * mm});
            skCircle(sketch, "E291", {"center": v(22.23, 22.86) * mm, "radius": 6 * mm});
            skCircle(sketch, "E292", {"center": v(60.32, 22.86) * mm, "radius": 6 * mm});
            skPoint(sketch, "E293.end.orphan", {"position": v(60.32, 20.63) * mm});
            skPoint(sketch, "E294.orphan", {"position": v(22.23, 21.05) * mm});
            skPoint(sketch, "E295.end.orphan", {"position": v(17.19, 22.86) * mm});
            skLineSegment(sketch, "E296", {"start": v(0, 63.5) * mm, "end": v(0, 55.56) * mm});
            skLineSegment(sketch, "E297", {"start": v(0, 63.5) * mm, "end": v(1.59, 63.5) * mm});
            skCircle(sketch, "E298", {"center": v(1.59, 7.94) * mm, "radius": 1.09 * mm});
            skCircle(sketch, "E299.MirrorC", {"center": v(1.59, 55.56) * mm, "radius": 1.09 * mm});
            skCircle(sketch, "E300.MirrorC", {"center": v(80.96, 55.56) * mm, "radius": 1.09 * mm});
            skCircle(sketch, "E301.MirrorC", {"center": v(80.96, 7.94) * mm, "radius": 1.09 * mm});
            skPoint(sketch, "E302.MirrorCS.start.orphan", {"position": v(0, 55.56) * mm});
            skPoint(sketch, "E303.start.orphan", {"position": v(0, 7.94) * mm});
            skPoint(sketch, "E304.end.orphan", {"position": v(41.27, 60.47) * mm});
            skSolve(sketch);
        }
        {
            var Q0;
            Q0=makeQuery(id+"F6.imprint","IMPRINT",FACE,{"disambiguationData":[TD([[makeQuery(id+"F6.imprint","IMPRINT",EDGE,{"derivedFrom":sQuery(id+"F6.wireOp",EDGE,"E242.top")}),-1.0]])]});
            extrude(context, id + "F7", {"entities" : qUnion([Q0]), "depth" : 3.17 * mm, "offsetDistance" : 25.4 * mm});
        }
        {
            var Q0;
            Q0=makeQuery(id+"F7.opExtrude","SWEPT_BODY",BODY,{"disambiguationData":[OSD([sQuery(id+"F6.wireOp",EDGE,"E242.top"),sQuery(id+"F6.wireOp",EDGE,"E242.right"),sQuery(id+"F6.wireOp",EDGE,"E243"),sQuery(id+"F6.wireOp",EDGE,"E244"),sQuery(id+"F6.wireOp",EDGE,"E245"),sQuery(id+"F6.wireOp",EDGE,"E246.MirrorCS"),sQuery(id+"F6.wireOp",EDGE,"E247.MirrorCS"),sQuery(id+"F6.wireOp",EDGE,"E248.MirrorCS"),sQuery(id+"F6.wireOp",EDGE,"E250.MirrorCS"),sQuery(id+"F6.wireOp",EDGE,"E251.MirrorCS"),sQuery(id+"F6.wireOp",EDGE,"E252.MirrorCS"),sQuery(id+"F6.wireOp",EDGE,"E253.MirrorCS"),sQuery(id+"F6.wireOp",EDGE,"E254.MirrorCS"),sQuery(id+"F6.wireOp",EDGE,"E255.MirrorCS"),sQuery(id+"F6.wireOp",EDGE,"E256.trimOffspring"),sQuery(id+"F6.wireOp",EDGE,"E259.trimOffspring"),sQuery(id+"F6.wireOp",EDGE,"E260.trimOffspring"),sQuery(id+"F6.wireOp",EDGE,"E261.trimOffspring"),sQuery(id+"F6.wireOp",EDGE,"E262.trimOffspring"),sQuery(id+"F6.wireOp",EDGE,"E264"),sQuery(id+"F6.wireOp",EDGE,"E265"),sQuery(id+"F6.wireOp",EDGE,"E266"),sQuery(id+"F6.wireOp",EDGE,"E267.MirrorCS"),sQuery(id+"F6.wireOp",EDGE,"E268.MirrorCS"),sQuery(id+"F6.wireOp",EDGE,"E270.MirrorCS"),sQuery(id+"F6.wireOp",EDGE,"E271.MirrorCS"),sQuery(id+"F6.wireOp",EDGE,"E272.MirrorCS"),sQuery(id+"F6.wireOp",EDGE,"E273.MirrorCS"),sQuery(id+"F6.wireOp",EDGE,"E274.MirrorCS"),sQuery(id+"F6.wireOp",EDGE,"E275.MirrorCS"),sQuery(id+"F6.wireOp",EDGE,"E276.MirrorCS"),sQuery(id+"F6.wireOp",EDGE,"E277.trimOffspring"),sQuery(id+"F6.wireOp",EDGE,"E278.trimOffspring"),sQuery(id+"F6.wireOp",EDGE,"E280.trimOffspring"),sQuery(id+"F6.wireOp",EDGE,"E281.trimOffspring"),sQuery(id+"F6.wireOp",EDGE,"E282.trimOffspring"),sQuery(id+"F6.wireOp",EDGE,"E284"),sQuery(id+"F6.wireOp",EDGE,"E283"),sQuery(id+"F6.wireOp",EDGE,"E285.trimOffspring"),sQuery(id+"F6.wireOp",EDGE,"E286.trimOffspring")])]});
            transform(context, id + "F8", {"entities" : qUnion([Q0]), "transformType" : TransformType.TRANSLATION_3D, "dx" : 0 * mm, "dy" : 0 * mm, "dz" : 53.97 * mm, "makeCopy" : false});
        }
        {
            var Q0;
            Q0=qCreatedBy(makeId("Right.planeOp"),FACE);
            var sketch = newSketch(context, id + "F9", { "sketchPlane" : qUnion([Q0])});
            skLineSegment(sketch, "E305.top", {"start": v(12.7, 57.15) * mm, "end": v(25.4, 57.15) * mm});
            skLineSegment(sketch, "E306", {"start": v(12.7, 3.17) * mm, "end": v(12.7, 0) * mm});
            skLineSegment(sketch, "E307", {"start": v(12.7, 0) * mm, "end": v(25.4, 0) * mm});
            skLineSegment(sketch, "E308", {"start": v(25.4, 0) * mm, "end": v(25.4, 3.18) * mm});
            skLineSegment(sketch, "E309", {"start": v(25.4, 3.18) * mm, "end": v(38.1, 3.18) * mm});
            skLineSegment(sketch, "E310.MirrorCS", {"start": v(38.1, 0) * mm, "end": v(38.1, 3.18) * mm});
            skLineSegment(sketch, "E311.MirrorCS", {"start": v(50.8, 3.17) * mm, "end": v(50.8, 0) * mm});
            skLineSegment(sketch, "E312.MirrorCS", {"start": v(50.8, 0) * mm, "end": v(38.1, 0) * mm});
            skLineSegment(sketch, "E313.MirrorCS", {"start": v(38.1, 3.18) * mm, "end": v(25.4, 3.18) * mm});
            skLineSegment(sketch, "E314.MirrorCS", {"start": v(60.32, 3.18) * mm, "end": v(57.15, 3.18) * mm});
            skLineSegment(sketch, "E315.MirrorCS", {"start": v(50.8, 53.98) * mm, "end": v(50.8, 57.15) * mm});
            skLineSegment(sketch, "E316.MirrorCS", {"start": v(38.1, 57.15) * mm, "end": v(38.1, 53.98) * mm});
            skLineSegment(sketch, "E317.MirrorCS", {"start": v(12.7, 53.98) * mm, "end": v(12.7, 57.15) * mm});
            skLineSegment(sketch, "E318.MirrorCS", {"start": v(25.4, 57.15) * mm, "end": v(25.4, 53.98) * mm});
            skLineSegment(sketch, "E319.MirrorCS", {"start": v(25.4, 53.98) * mm, "end": v(38.1, 53.98) * mm});
            skLineSegment(sketch, "E320.MirrorCS", {"start": v(38.1, 53.98) * mm, "end": v(25.4, 53.98) * mm});
            skLineSegment(sketch, "E321.MirrorCS", {"start": v(50.8, 57.15) * mm, "end": v(38.1, 57.15) * mm});
            skLineSegment(sketch, "E322.MirrorCS", {"start": v(60.32, 53.98) * mm, "end": v(56.7, 53.98) * mm});
            skLineSegment(sketch, "E323.MirrorCS", {"start": v(3.17, 53.98) * mm, "end": v(6.8, 53.98) * mm});
            skLineSegment(sketch, "E324.trimOffspring", {"start": v(38.1, 57.15) * mm, "end": v(50.8, 57.15) * mm});
            skPoint(sketch, "E325.orphan", {"position": v(31.75, 57.15) * mm});
            skPoint(sketch, "E326.MirrorCS.start.orphan", {"position": v(63.5, 57.15) * mm});
            skLineSegment(sketch, "E327.trimOffspring", {"start": v(38.1, 0) * mm, "end": v(50.8, 0) * mm});
            skPoint(sketch, "E328.MirrorCS.start.orphan", {"position": v(63.5, 0) * mm});
            skPoint(sketch, "E329.orphan", {"position": v(0, 57.15) * mm});
            skLineSegment(sketch, "E330", {"start": v(0, 15.87) * mm, "end": v(3.17, 15.87) * mm});
            skLineSegment(sketch, "E331.trimOffspring", {"start": v(0, 15.87) * mm, "end": v(0, 41.28) * mm});
            skLineSegment(sketch, "E332.MirrorCS", {"start": v(3.17, 41.28) * mm, "end": v(3.17, 46.53) * mm});
            skLineSegment(sketch, "E333.MirrorCS", {"start": v(0, 41.28) * mm, "end": v(0, 15.87) * mm});
            skLineSegment(sketch, "E334.MirrorCS", {"start": v(0, 41.28) * mm, "end": v(3.17, 41.28) * mm});
            skLineSegment(sketch, "E335.MirrorCS", {"start": v(63.5, 41.28) * mm, "end": v(60.32, 41.28) * mm});
            skLineSegment(sketch, "E336.MirrorCS", {"start": v(63.5, 15.87) * mm, "end": v(60.32, 15.87) * mm});
            skLineSegment(sketch, "E337.MirrorCS", {"start": v(60.32, 41.28) * mm, "end": v(60.32, 46.53) * mm});
            skLineSegment(sketch, "E338.MirrorCS", {"start": v(63.5, 15.87) * mm, "end": v(63.5, 41.28) * mm});
            skLineSegment(sketch, "E339.MirrorCS", {"start": v(60.32, 15.87) * mm, "end": v(60.32, 10.72) * mm});
            skLineSegment(sketch, "E340.MirrorCS", {"start": v(63.5, 41.28) * mm, "end": v(63.5, 15.87) * mm});
            skPoint(sketch, "E341.MirrorCS.end.orphan", {"position": v(58.61, 28.58) * mm});
            skPoint(sketch, "E341.MirrorCS.start.orphan", {"position": v(63.5, 28.58) * mm});
            skPoint(sketch, "E342.orphan", {"position": v(63.5, 3.17) * mm});
            skPoint(sketch, "E343.orphan", {"position": v(0, 3.17) * mm});
            skPoint(sketch, "E344.end.orphan", {"position": v(4.89, 28.58) * mm});
            skPoint(sketch, "E344.start.orphan", {"position": v(0, 28.58) * mm});
            skPoint(sketch, "E305.left.start.orphan", {"position": v(0, 0) * mm});
            skPoint(sketch, "E345", {"position": v(13.33, 3.17) * mm});
            skLineSegment(sketch, "E346", {"start": v(57.15, 3.18) * mm, "end": v(57.15, 3.23) * mm});
            skLineSegment(sketch, "E347.bottom", {"start": v(57.15, 7.62) * mm, "end": v(48.26, 7.62) * mm});
            skLineSegment(sketch, "E347.top", {"start": v(57.15, 19.05) * mm, "end": v(48.26, 19.05) * mm});
            skLineSegment(sketch, "E347.left", {"start": v(57.15, 7.62) * mm, "end": v(57.15, 19.05) * mm});
            skLineSegment(sketch, "E347.right", {"start": v(48.26, 7.62) * mm, "end": v(48.26, 19.05) * mm});
            skLineSegment(sketch, "E348.bottom", {"start": v(22.22, 6.35) * mm, "end": v(14.22, 6.35) * mm});
            skLineSegment(sketch, "E348.top", {"start": v(22.22, 10.54) * mm, "end": v(14.22, 10.54) * mm});
            skLineSegment(sketch, "E348.left", {"start": v(22.22, 6.35) * mm, "end": v(22.22, 10.54) * mm});
            skLineSegment(sketch, "E348.right", {"start": v(14.22, 6.35) * mm, "end": v(14.22, 10.54) * mm});
            skLineSegment(sketch, "E349.top", {"start": v(12.7, 57.2) * mm, "end": v(25.4, 57.2) * mm});
            skLineSegment(sketch, "E350", {"start": v(3.17, 3.23) * mm, "end": v(6.8, 3.23) * mm});
            skLineSegment(sketch, "E351", {"start": v(12.7, 3.23) * mm, "end": v(12.7, 0.05) * mm});
            skLineSegment(sketch, "E352", {"start": v(12.7, 0.05) * mm, "end": v(25.4, 0.05) * mm});
            skLineSegment(sketch, "E353", {"start": v(25.4, 0.05) * mm, "end": v(25.4, 3.23) * mm});
            skLineSegment(sketch, "E354", {"start": v(25.4, 3.23) * mm, "end": v(38.1, 3.23) * mm});
            skLineSegment(sketch, "E355.MirrorCS", {"start": v(38.1, 0.05) * mm, "end": v(38.1, 3.23) * mm});
            skLineSegment(sketch, "E356.MirrorCS", {"start": v(50.8, 3.23) * mm, "end": v(50.8, 0.05) * mm});
            skLineSegment(sketch, "E357.MirrorCS", {"start": v(50.8, 0.05) * mm, "end": v(38.1, 0.05) * mm});
            skLineSegment(sketch, "E358.MirrorCS", {"start": v(38.1, 3.23) * mm, "end": v(25.4, 3.23) * mm});
            skLineSegment(sketch, "E359.MirrorCS", {"start": v(50.8, 54.03) * mm, "end": v(50.8, 57.2) * mm});
            skLineSegment(sketch, "E360.MirrorCS", {"start": v(38.1, 57.2) * mm, "end": v(38.1, 54.03) * mm});
            skLineSegment(sketch, "E361.MirrorCS", {"start": v(12.7, 54.03) * mm, "end": v(12.7, 57.2) * mm});
            skLineSegment(sketch, "E362.MirrorCS", {"start": v(25.4, 57.2) * mm, "end": v(25.4, 54.03) * mm});
            skLineSegment(sketch, "E363.MirrorCS", {"start": v(25.4, 54.03) * mm, "end": v(38.1, 54.03) * mm});
            skLineSegment(sketch, "E364.MirrorCS", {"start": v(38.1, 54.03) * mm, "end": v(25.4, 54.03) * mm});
            skLineSegment(sketch, "E365.MirrorCS", {"start": v(50.8, 57.2) * mm, "end": v(38.1, 57.2) * mm});
            skLineSegment(sketch, "E366.MirrorCS", {"start": v(60.32, 54.03) * mm, "end": v(56.7, 54.03) * mm});
            skLineSegment(sketch, "E367.MirrorCS", {"start": v(3.17, 54.03) * mm, "end": v(6.8, 54.03) * mm});
            skLineSegment(sketch, "E368.trimOffspring", {"start": v(38.1, 57.2) * mm, "end": v(50.8, 57.2) * mm});
            skPoint(sketch, "E369.orphan", {"position": v(31.75, 57.2) * mm});
            skPoint(sketch, "E370.MirrorCS.start.orphan", {"position": v(63.5, 57.2) * mm});
            skLineSegment(sketch, "E371.trimOffspring", {"start": v(38.1, 0.05) * mm, "end": v(50.8, 0.05) * mm});
            skPoint(sketch, "E372.MirrorCS.start.orphan", {"position": v(63.5, 0.05) * mm});
            skPoint(sketch, "E373.orphan", {"position": v(0, 57.2) * mm});
            skLineSegment(sketch, "E374", {"start": v(0, 15.93) * mm, "end": v(3.17, 15.93) * mm});
            skLineSegment(sketch, "E375", {"start": v(3.17, 15.93) * mm, "end": v(3.17, 10.72) * mm});
            skLineSegment(sketch, "E376.trimOffspring", {"start": v(0, 15.93) * mm, "end": v(0, 41.33) * mm});
            skLineSegment(sketch, "E377.MirrorCS", {"start": v(3.17, 41.33) * mm, "end": v(3.17, 46.53) * mm});
            skLineSegment(sketch, "E378.MirrorCS", {"start": v(0, 41.33) * mm, "end": v(0, 15.93) * mm});
            skLineSegment(sketch, "E379.MirrorCS", {"start": v(0, 41.33) * mm, "end": v(3.17, 41.33) * mm});
            skLineSegment(sketch, "E380.MirrorCS", {"start": v(63.5, 41.33) * mm, "end": v(60.32, 41.33) * mm});
            skLineSegment(sketch, "E381.MirrorCS", {"start": v(63.5, 15.93) * mm, "end": v(60.32, 15.93) * mm});
            skLineSegment(sketch, "E382.MirrorCS", {"start": v(60.32, 41.33) * mm, "end": v(60.32, 46.53) * mm});
            skLineSegment(sketch, "E383.MirrorCS", {"start": v(63.5, 15.93) * mm, "end": v(63.5, 41.33) * mm});
            skLineSegment(sketch, "E384.MirrorCS", {"start": v(60.32, 15.93) * mm, "end": v(60.32, 10.72) * mm});
            skLineSegment(sketch, "E385.MirrorCS", {"start": v(63.5, 41.33) * mm, "end": v(63.5, 15.93) * mm});
            skPoint(sketch, "E386.MirrorCS.end.orphan", {"position": v(58.61, 28.63) * mm});
            skPoint(sketch, "E386.MirrorCS.start.orphan", {"position": v(63.5, 28.63) * mm});
            skPoint(sketch, "E387.orphan", {"position": v(63.5, 3.23) * mm});
            skPoint(sketch, "E388.orphan", {"position": v(0, 3.23) * mm});
            skPoint(sketch, "E389.end.orphan", {"position": v(4.89, 28.63) * mm});
            skPoint(sketch, "E389.start.orphan", {"position": v(0, 28.63) * mm});
            skPoint(sketch, "E349.left.start.orphan", {"position": v(0, 0.05) * mm});
            skLineSegment(sketch, "E390.top", {"start": v(56.7, 6.4) * mm, "end": v(54.42, 6.4) * mm});
            skLineSegment(sketch, "E390.left", {"start": v(56.7, 3.23) * mm, "end": v(56.7, 4.88) * mm});
            skLineSegment(sketch, "E390.right", {"start": v(54.42, 3.23) * mm, "end": v(54.42, 4.88) * mm});
            skPoint(sketch, "E391.end.orphan", {"position": v(54.42, 3.23) * mm});
            skLineSegment(sketch, "E392.trimOffspring", {"start": v(54.42, 3.23) * mm, "end": v(50.8, 3.23) * mm});
            skPoint(sketch, "E393.start.orphan", {"position": v(55.56, 3.23) * mm});
            skLineSegment(sketch, "E394", {"start": v(56.7, 3.23) * mm, "end": v(60.32, 3.23) * mm});
            skLineSegment(sketch, "E395.bottom", {"start": v(57.91, 6.4) * mm, "end": v(53.21, 6.4) * mm});
            skLineSegment(sketch, "E395.top", {"start": v(57.91, 4.88) * mm, "end": v(56.7, 4.88) * mm});
            skLineSegment(sketch, "E395.left", {"start": v(57.91, 6.4) * mm, "end": v(57.91, 4.88) * mm});
            skLineSegment(sketch, "E395.right", {"start": v(53.21, 6.4) * mm, "end": v(53.21, 4.88) * mm});
            skPoint(sketch, "E395.middle", {"position": v(55.56, 5.64) * mm});
            skLineSegment(sketch, "E396.trimOffspring", {"start": v(54.42, 4.88) * mm, "end": v(53.21, 4.88) * mm});
            skPoint(sketch, "E397.start.orphan", {"position": v(55.56, 6.4) * mm});
            skLineSegment(sketch, "E398.MirrorCS", {"start": v(54.42, 52.38) * mm, "end": v(53.21, 52.38) * mm});
            skLineSegment(sketch, "E399.MirrorCS", {"start": v(57.91, 52.38) * mm, "end": v(56.7, 52.38) * mm});
            skLineSegment(sketch, "E400.MirrorCS", {"start": v(56.7, 54.03) * mm, "end": v(56.7, 52.38) * mm});
            skLineSegment(sketch, "E401.MirrorCS", {"start": v(54.42, 54.03) * mm, "end": v(54.42, 52.38) * mm});
            skLineSegment(sketch, "E402.MirrorCS", {"start": v(56.7, 50.85) * mm, "end": v(54.42, 50.85) * mm});
            skLineSegment(sketch, "E403.MirrorCS", {"start": v(53.21, 50.85) * mm, "end": v(53.21, 52.38) * mm});
            skPoint(sketch, "E404.MirrorP", {"position": v(54.42, 54.03) * mm});
            skPoint(sketch, "E405.MirrorP", {"position": v(55.56, 50.85) * mm});
            skLineSegment(sketch, "E406.MirrorCS", {"start": v(57.91, 50.85) * mm, "end": v(53.21, 50.85) * mm});
            skLineSegment(sketch, "E407.MirrorCS", {"start": v(57.91, 50.85) * mm, "end": v(57.91, 52.38) * mm});
            skPoint(sketch, "E408.MirrorP", {"position": v(55.56, 54.03) * mm});
            skPoint(sketch, "E409.MirrorP", {"position": v(55.56, 51.61) * mm});
            skLineSegment(sketch, "E410.MirrorCS", {"start": v(6.8, 6.4) * mm, "end": v(9.08, 6.4) * mm});
            skLineSegment(sketch, "E411.MirrorCS", {"start": v(9.08, 4.88) * mm, "end": v(10.29, 4.88) * mm});
            skLineSegment(sketch, "E412.MirrorCS", {"start": v(9.08, 3.23) * mm, "end": v(9.08, 4.88) * mm});
            skLineSegment(sketch, "E413.MirrorCS", {"start": v(6.8, 3.23) * mm, "end": v(6.8, 4.88) * mm});
            skLineSegment(sketch, "E414.MirrorCS", {"start": v(5.59, 4.88) * mm, "end": v(6.8, 4.88) * mm});
            skLineSegment(sketch, "E415.MirrorCS", {"start": v(6.8, 3.23) * mm, "end": v(3.17, 3.23) * mm});
            skPoint(sketch, "E416.MirrorP", {"position": v(7.94, 6.4) * mm});
            skLineSegment(sketch, "E417.MirrorCS", {"start": v(9.08, 3.23) * mm, "end": v(12.7, 3.23) * mm});
            skLineSegment(sketch, "E418.MirrorCS", {"start": v(5.59, 6.4) * mm, "end": v(10.29, 6.4) * mm});
            skPoint(sketch, "E419.MirrorP", {"position": v(9.08, 3.23) * mm});
            skPoint(sketch, "E420.MirrorP", {"position": v(7.94, 5.64) * mm});
            skLineSegment(sketch, "E421.MirrorCS", {"start": v(5.59, 6.4) * mm, "end": v(5.59, 4.88) * mm});
            skLineSegment(sketch, "E422.MirrorCS", {"start": v(10.29, 6.4) * mm, "end": v(10.29, 4.88) * mm});
            skPoint(sketch, "E423.MirrorP", {"position": v(7.94, 3.23) * mm});
            skLineSegment(sketch, "E424.MirrorCS", {"start": v(6.8, 50.85) * mm, "end": v(9.08, 50.85) * mm});
            skLineSegment(sketch, "E425.MirrorCS", {"start": v(10.29, 50.85) * mm, "end": v(10.29, 52.38) * mm});
            skLineSegment(sketch, "E426.MirrorCS", {"start": v(9.08, 52.38) * mm, "end": v(10.29, 52.38) * mm});
            skLineSegment(sketch, "E427.MirrorCS", {"start": v(6.8, 54.03) * mm, "end": v(6.8, 52.38) * mm});
            skPoint(sketch, "E428.MirrorP", {"position": v(7.94, 51.61) * mm});
            skLineSegment(sketch, "E429.MirrorCS", {"start": v(5.59, 50.85) * mm, "end": v(10.29, 50.85) * mm});
            skLineSegment(sketch, "E430.MirrorCS", {"start": v(5.59, 50.85) * mm, "end": v(5.59, 52.38) * mm});
            skLineSegment(sketch, "E431.MirrorCS", {"start": v(5.59, 52.38) * mm, "end": v(6.8, 52.38) * mm});
            skPoint(sketch, "E432.MirrorP", {"position": v(9.08, 54.03) * mm});
            skPoint(sketch, "E433.MirrorP", {"position": v(7.94, 50.85) * mm});
            skPoint(sketch, "E434.MirrorP", {"position": v(7.94, 54.03) * mm});
            skLineSegment(sketch, "E435.MirrorCS", {"start": v(9.08, 54.03) * mm, "end": v(9.08, 52.38) * mm});
            skLineSegment(sketch, "E436.trimOffspring", {"start": v(54.42, 54.03) * mm, "end": v(50.8, 54.03) * mm});
            skLineSegment(sketch, "E437.trimOffspring", {"start": v(9.08, 54.03) * mm, "end": v(12.7, 54.03) * mm});
            skPoint(sketch, "E438.MirrorCS.start.orphan", {"position": v(3.17, 54.03) * mm});
            skLineSegment(sketch, "E439.bottom", {"start": v(60.32, 10.72) * mm, "end": v(58.67, 10.72) * mm});
            skLineSegment(sketch, "E439.top", {"start": v(60.32, 8.43) * mm, "end": v(58.67, 8.43) * mm});
            skLineSegment(sketch, "E439.right", {"start": v(57.15, 10.72) * mm, "end": v(57.15, 8.43) * mm});
            skLineSegment(sketch, "E440.bottom", {"start": v(57.15, 7.23) * mm, "end": v(58.67, 7.23) * mm});
            skLineSegment(sketch, "E440.top", {"start": v(57.15, 11.93) * mm, "end": v(58.67, 11.93) * mm});
            skLineSegment(sketch, "E440.left", {"start": v(57.15, 7.23) * mm, "end": v(57.15, 11.93) * mm});
            skLineSegment(sketch, "E440.right", {"start": v(58.67, 7.23) * mm, "end": v(58.67, 8.43) * mm});
            skPoint(sketch, "E440.middle", {"position": v(57.91, 9.58) * mm});
            skLineSegment(sketch, "E441.trimOffspring", {"start": v(58.67, 10.72) * mm, "end": v(58.67, 11.93) * mm});
            skPoint(sketch, "E442.start.orphan", {"position": v(57.15, 9.58) * mm});
            skLineSegment(sketch, "E443.trimOffspring", {"start": v(60.32, 8.43) * mm, "end": v(60.32, 3.23) * mm});
            skPoint(sketch, "E444.orphan", {"position": v(60.32, 8.43) * mm});
            skPoint(sketch, "E439.left.end.orphan", {"position": v(60.32, 9.58) * mm});
            skPoint(sketch, "E445.MirrorP", {"position": v(57.91, 47.68) * mm});
            skPoint(sketch, "E446.MirrorP", {"position": v(57.15, 47.68) * mm});
            skLineSegment(sketch, "E447.MirrorCS", {"start": v(57.15, 46.53) * mm, "end": v(57.15, 48.82) * mm});
            skLineSegment(sketch, "E448.MirrorCS", {"start": v(57.15, 45.33) * mm, "end": v(58.67, 45.33) * mm});
            skLineSegment(sketch, "E449.MirrorCS", {"start": v(57.15, 50.03) * mm, "end": v(57.15, 45.33) * mm});
            skLineSegment(sketch, "E450.MirrorCS", {"start": v(60.32, 48.82) * mm, "end": v(58.67, 48.82) * mm});
            skLineSegment(sketch, "E451.MirrorCS", {"start": v(57.15, 50.03) * mm, "end": v(58.67, 50.03) * mm});
            skLineSegment(sketch, "E452.MirrorCS", {"start": v(60.32, 46.53) * mm, "end": v(58.67, 46.53) * mm});
            skLineSegment(sketch, "E453.MirrorCS", {"start": v(58.67, 50.03) * mm, "end": v(58.67, 48.82) * mm});
            skLineSegment(sketch, "E454.MirrorCS", {"start": v(58.67, 46.53) * mm, "end": v(58.67, 45.33) * mm});
            skLineSegment(sketch, "E455.MirrorCS", {"start": v(6.35, 46.53) * mm, "end": v(6.35, 48.82) * mm});
            skLineSegment(sketch, "E456.MirrorCS", {"start": v(6.35, 50.03) * mm, "end": v(4.83, 50.03) * mm});
            skLineSegment(sketch, "E457.MirrorCS", {"start": v(6.35, 50.03) * mm, "end": v(6.35, 45.33) * mm});
            skPoint(sketch, "E458.MirrorP", {"position": v(5.59, 47.68) * mm});
            skLineSegment(sketch, "E459.MirrorCS", {"start": v(4.83, 46.53) * mm, "end": v(4.83, 45.33) * mm});
            skLineSegment(sketch, "E460.MirrorCS", {"start": v(3.17, 46.53) * mm, "end": v(4.83, 46.53) * mm});
            skLineSegment(sketch, "E461.MirrorCS", {"start": v(4.83, 50.03) * mm, "end": v(4.83, 48.82) * mm});
            skLineSegment(sketch, "E462.MirrorCS", {"start": v(3.17, 48.82) * mm, "end": v(4.83, 48.82) * mm});
            skLineSegment(sketch, "E463.MirrorCS", {"start": v(6.35, 45.33) * mm, "end": v(4.83, 45.33) * mm});
            skPoint(sketch, "E464.MirrorP", {"position": v(6.35, 47.68) * mm});
            skPoint(sketch, "E465.MirrorP", {"position": v(5.59, 9.58) * mm});
            skPoint(sketch, "E466.MirrorP", {"position": v(6.35, 9.58) * mm});
            skLineSegment(sketch, "E467.MirrorCS", {"start": v(6.35, 10.72) * mm, "end": v(6.35, 8.43) * mm});
            skLineSegment(sketch, "E468.MirrorCS", {"start": v(3.17, 8.43) * mm, "end": v(4.83, 8.43) * mm});
            skLineSegment(sketch, "E469.MirrorCS", {"start": v(6.35, 7.23) * mm, "end": v(6.35, 11.93) * mm});
            skLineSegment(sketch, "E470.MirrorCS", {"start": v(4.83, 10.72) * mm, "end": v(4.83, 11.93) * mm});
            skPoint(sketch, "E471.MirrorP", {"position": v(3.17, 9.58) * mm});
            skLineSegment(sketch, "E472.MirrorCS", {"start": v(3.17, 8.43) * mm, "end": v(3.17, 3.23) * mm});
            skLineSegment(sketch, "E473.MirrorCS", {"start": v(3.17, 10.72) * mm, "end": v(4.83, 10.72) * mm});
            skLineSegment(sketch, "E474.MirrorCS", {"start": v(4.83, 7.23) * mm, "end": v(4.83, 8.43) * mm});
            skLineSegment(sketch, "E475.MirrorCS", {"start": v(6.35, 7.23) * mm, "end": v(4.83, 7.23) * mm});
            skLineSegment(sketch, "E476.MirrorCS", {"start": v(6.35, 11.93) * mm, "end": v(4.83, 11.93) * mm});
            skPoint(sketch, "E477.MirrorP", {"position": v(3.17, 8.43) * mm});
            skLineSegment(sketch, "E478.trimOffspring", {"start": v(60.32, 48.82) * mm, "end": v(60.32, 54.03) * mm});
            skLineSegment(sketch, "E479.trimOffspring", {"start": v(3.17, 48.82) * mm, "end": v(3.17, 54.03) * mm});
            skPoint(sketch, "E480.start.orphan", {"position": v(31.75, 3.23) * mm});
            skLineSegment(sketch, "E481.trimOffspring", {"start": v(57.15, 7.23) * mm, "end": v(57.15, 7.62) * mm});
            skLineSegment(sketch, "E482.trimOffspring", {"start": v(60.32, 8.43) * mm, "end": v(60.32, 3.18) * mm});
            skLineSegment(sketch, "E483.trimOffspring", {"start": v(60.32, 48.82) * mm, "end": v(60.32, 53.98) * mm});
            skLineSegment(sketch, "E484.trimOffspring", {"start": v(54.42, 53.98) * mm, "end": v(50.8, 53.98) * mm});
            skLineSegment(sketch, "E485.trimOffspring", {"start": v(9.08, 53.98) * mm, "end": v(12.7, 53.98) * mm});
            skLineSegment(sketch, "E486.trimOffspring", {"start": v(3.17, 48.82) * mm, "end": v(3.17, 53.98) * mm});
            skLineSegment(sketch, "E487.trimOffspring", {"start": v(3.17, 9.58) * mm, "end": v(3.17, 3.18) * mm});
            skSolve(sketch);
        }
        {
            var Q0;
            {var subQ53=sQuery(id+"F9.wireOp",EDGE,"E315.MirrorCS");Q0=makeQuery(id+"F9.imprint","IMPRINT",FACE,{"disambiguationData":[TD([[makeQuery(id+"F9.imprint","IMPRINT",EDGE,{"derivedFrom":subQ53}),1.0]])]});}
            extrude(context, id + "F10", {"entities" : qUnion([Q0]), "depth" : 3.17 * mm, "offsetDistance" : 25.4 * mm});
        }
        {
            var Q0;
            Q0=makeQuery(id+"F10.opExtrude","SWEPT_BODY",BODY,{"disambiguationData":[OSD([sQuery(id+"F9.wireOp",EDGE,"309e3afe-a993-452b-95af-8ca9c9179dc3"),sQuery(id+"F9.wireOp",EDGE,"E306"),sQuery(id+"F9.wireOp",EDGE,"E307"),sQuery(id+"F9.wireOp",EDGE,"E308"),sQuery(id+"F9.wireOp",EDGE,"E310.MirrorCS"),sQuery(id+"F9.wireOp",EDGE,"E311.MirrorCS"),sQuery(id+"F9.wireOp",EDGE,"E313.MirrorCS"),sQuery(id+"F9.wireOp",EDGE,"E314.MirrorCS"),sQuery(id+"F9.wireOp",EDGE,"E315.MirrorCS"),sQuery(id+"F9.wireOp",EDGE,"E316.MirrorCS"),sQuery(id+"F9.wireOp",EDGE,"E317.MirrorCS"),sQuery(id+"F9.wireOp",EDGE,"E318.MirrorCS"),sQuery(id+"F9.wireOp",EDGE,"E320.MirrorCS"),sQuery(id+"F9.wireOp",EDGE,"E322.MirrorCS"),sQuery(id+"F9.wireOp",EDGE,"E305.top"),sQuery(id+"F9.wireOp",EDGE,"E323.MirrorCS"),sQuery(id+"F9.wireOp",EDGE,"E327.trimOffspring"),sQuery(id+"F9.wireOp",EDGE,"E324.trimOffspring"),sQuery(id+"F9.wireOp",EDGE,"E330"),sQuery(id+"F9.wireOp",EDGE,"38c27faf-0178-4be6-b48d-b3d4dc0c8408"),sQuery(id+"F9.wireOp",EDGE,"E332.MirrorCS"),sQuery(id+"F9.wireOp",EDGE,"E333.MirrorCS"),sQuery(id+"F9.wireOp",EDGE,"E334.MirrorCS"),sQuery(id+"F9.wireOp",EDGE,"E335.MirrorCS"),sQuery(id+"F9.wireOp",EDGE,"E336.MirrorCS"),sQuery(id+"F9.wireOp",EDGE,"E339.MirrorCS"),sQuery(id+"F9.wireOp",EDGE,"E337.MirrorCS"),sQuery(id+"F9.wireOp",EDGE,"E338.MirrorCS")])]});
            transform(context, id + "F11", {"entities" : qUnion([Q0]), "transformType" : TransformType.TRANSLATION_3D, "dx" : 79.38 * mm, "dy" : 0 * mm, "dz" : 0 * mm, "makeCopy" : false});
        }
        {
            var Q0;
            Q0=qCreatedBy(makeId("Front.planeOp"),FACE);
            var sketch = newSketch(context, id + "F12", { "sketchPlane" : qUnion([Q0])});
            skLineSegment(sketch, "E488.bottom", {"start": v(3.17, 0) * mm, "end": v(28.58, 0) * mm});
            skLineSegment(sketch, "E488.top", {"start": v(3.17, 57.15) * mm, "end": v(28.58, 57.15) * mm});
            skLineSegment(sketch, "E489.top", {"start": v(0, 3.18) * mm, "end": v(3.17, 3.18) * mm});
            skLineSegment(sketch, "E489.right", {"start": v(3.17, 0) * mm, "end": v(3.17, 3.18) * mm});
            skLineSegment(sketch, "E490.top", {"start": v(28.58, 3.18) * mm, "end": v(53.98, 3.18) * mm});
            skLineSegment(sketch, "E490.left", {"start": v(28.58, 0) * mm, "end": v(28.58, 3.18) * mm});
            skLineSegment(sketch, "E490.right", {"start": v(53.98, 0) * mm, "end": v(53.98, 3.18) * mm});
            skPoint(sketch, "E491.endSnap0", {"position": v(41.28, 3.18) * mm});
            skLineSegment(sketch, "E492.MirrorCS", {"start": v(82.55, 3.18) * mm, "end": v(79.38, 3.18) * mm});
            skLineSegment(sketch, "E493.MirrorCS", {"start": v(79.38, 0) * mm, "end": v(79.38, 3.18) * mm});
            skLineSegment(sketch, "E494.MirrorCS", {"start": v(82.55, 53.98) * mm, "end": v(79.38, 53.98) * mm});
            skLineSegment(sketch, "E495.MirrorCS", {"start": v(53.98, 57.15) * mm, "end": v(53.98, 53.98) * mm});
            skLineSegment(sketch, "E496.MirrorCS", {"start": v(28.58, 57.15) * mm, "end": v(28.58, 53.98) * mm});
            skLineSegment(sketch, "E497.MirrorCS", {"start": v(0, 53.98) * mm, "end": v(3.17, 53.98) * mm});
            skLineSegment(sketch, "E498.MirrorCS", {"start": v(3.17, 57.15) * mm, "end": v(3.17, 53.98) * mm});
            skLineSegment(sketch, "E499.MirrorCS", {"start": v(79.38, 57.15) * mm, "end": v(79.38, 53.98) * mm});
            skLineSegment(sketch, "E500.MirrorCS", {"start": v(28.58, 53.98) * mm, "end": v(53.98, 53.98) * mm});
            skPoint(sketch, "E501.MirrorP", {"position": v(41.28, 53.98) * mm});
            skPoint(sketch, "E502.orphan", {"position": v(0, 57.15) * mm});
            skPoint(sketch, "E503.orphan", {"position": v(82.55, 57.15) * mm});
            skPoint(sketch, "E504.start.orphan", {"position": v(0, 28.57) * mm});
            skPoint(sketch, "E505.MirrorCS.start.orphan", {"position": v(82.55, 0) * mm});
            skLineSegment(sketch, "E506.trimOffspring", {"start": v(53.98, 57.15) * mm, "end": v(79.38, 57.15) * mm});
            skLineSegment(sketch, "E507", {"start": v(53.98, 0) * mm, "end": v(79.38, 0) * mm});
            skLineSegment(sketch, "E508", {"start": v(0, 3.18) * mm, "end": v(0, 15.88) * mm});
            skLineSegment(sketch, "E509.bottom", {"start": v(0, 15.88) * mm, "end": v(3.18, 15.88) * mm});
            skLineSegment(sketch, "E509.top", {"start": v(0, 41.28) * mm, "end": v(3.17, 41.28) * mm});
            skLineSegment(sketch, "E509.right", {"start": v(3.17, 15.87) * mm, "end": v(3.17, 41.28) * mm});
            skLineSegment(sketch, "E510.trimOffspring", {"start": v(0, 41.28) * mm, "end": v(0, 53.98) * mm});
            skLineSegment(sketch, "E511.MirrorCS", {"start": v(82.55, 41.28) * mm, "end": v(82.55, 53.98) * mm});
            skLineSegment(sketch, "E512.MirrorCS", {"start": v(79.38, 57.15) * mm, "end": v(53.98, 57.15) * mm});
            skLineSegment(sketch, "E513.MirrorCS", {"start": v(82.55, 15.88) * mm, "end": v(79.38, 15.88) * mm});
            skLineSegment(sketch, "E514.MirrorCS", {"start": v(82.55, 41.28) * mm, "end": v(79.38, 41.28) * mm});
            skLineSegment(sketch, "E515.MirrorCS", {"start": v(79.38, 0) * mm, "end": v(53.98, 0) * mm});
            skLineSegment(sketch, "E516.MirrorCS", {"start": v(82.55, 3.17) * mm, "end": v(82.55, 15.87) * mm});
            skPoint(sketch, "E517.MirrorP", {"position": v(82.55, 28.57) * mm});
            skLineSegment(sketch, "E518.MirrorCS", {"start": v(79.38, 15.87) * mm, "end": v(79.38, 41.28) * mm});
            skLineSegment(sketch, "E519.MirrorCS", {"start": v(82.55, 3.18) * mm, "end": v(82.55, 15.88) * mm});
            skPoint(sketch, "E520.orphan", {"position": v(28.58, 0) * mm});
            skPoint(sketch, "E491.end.orphan", {"position": v(41.28, 6.6) * mm});
            skPoint(sketch, "E491.start.orphan", {"position": v(41.28, 3.18) * mm});
            skPoint(sketch, "E521.orphan", {"position": v(0, 0) * mm});
            skLineSegment(sketch, "E522", {"start": v(0, 0) * mm, "end": v(0, 9.53) * mm});
            skLineSegment(sketch, "E523", {"start": v(0, 0) * mm, "end": v(1.59, 0) * mm});
            skCircle(sketch, "E524", {"center": v(1.59, 9.52) * mm, "radius": 1.14 * mm});
            skPoint(sketch, "E524.centerSnap0", {"position": v(1.59, 3.18) * mm});
            skPoint(sketch, "E525.endSnap0", {"position": v(3.17, 28.58) * mm});
            skPoint(sketch, "E526.endSnap0", {"position": v(41.27, 53.98) * mm});
            skCircle(sketch, "E527.MirrorC", {"center": v(1.59, 47.63) * mm, "radius": 1.14 * mm});
            skCircle(sketch, "E528.MirrorC", {"center": v(80.96, 47.63) * mm, "radius": 1.14 * mm});
            skCircle(sketch, "E529.MirrorC", {"center": v(80.96, 9.52) * mm, "radius": 1.14 * mm});
            skPoint(sketch, "E525.end.orphan", {"position": v(1.54, 28.58) * mm});
            skPoint(sketch, "E525.start.orphan", {"position": v(3.17, 28.58) * mm});
            skPoint(sketch, "E526.end.orphan", {"position": v(41.27, 55.6) * mm});
            skPoint(sketch, "E526.start.orphan", {"position": v(41.27, 53.98) * mm});
            skPoint(sketch, "E530.end.orphan", {"position": v(0, 9.52) * mm});
            skSolve(sketch);
        }
        {
            var Q0;
            Q0 = qSketchRegion(id + "F12", true);
            extrude(context, id + "F13", {"entities" : qUnion([Q0]), "oppositeDirection" : true, "depth" : 3.17 * mm, "offsetDistance" : 25.4 * mm});
        }
        {
            var Q0;
            Q0=makeQuery(id+"F13.opExtrude","SWEPT_BODY",BODY,{"disambiguationData":[OSD([sQuery(id+"F12.wireOp",EDGE,"E489.top"),sQuery(id+"F12.wireOp",EDGE,"E489.right"),sQuery(id+"F12.wireOp",EDGE,"E488.bottom"),sQuery(id+"F12.wireOp",EDGE,"E490.top"),sQuery(id+"F12.wireOp",EDGE,"E490.left"),sQuery(id+"F12.wireOp",EDGE,"E490.right"),sQuery(id+"F12.wireOp",EDGE,"E495.MirrorCS"),sQuery(id+"F12.wireOp",EDGE,"E496.MirrorCS"),sQuery(id+"F12.wireOp",EDGE,"E497.MirrorCS"),sQuery(id+"F12.wireOp",EDGE,"E498.MirrorCS"),sQuery(id+"F12.wireOp",EDGE,"E500.MirrorCS"),sQuery(id+"F12.wireOp",EDGE,"E488.top"),sQuery(id+"F12.wireOp",EDGE,"E508"),sQuery(id+"F12.wireOp",EDGE,"E509.bottom"),sQuery(id+"F12.wireOp",EDGE,"E509.top"),sQuery(id+"F12.wireOp",EDGE,"E509.right"),sQuery(id+"F12.wireOp",EDGE,"E510.trimOffspring"),sQuery(id+"F12.wireOp",EDGE,"E512.MirrorCS"),sQuery(id+"F12.wireOp",EDGE,"E494.MirrorCS"),sQuery(id+"F12.wireOp",EDGE,"E492.MirrorCS"),sQuery(id+"F12.wireOp",EDGE,"E493.MirrorCS"),sQuery(id+"F12.wireOp",EDGE,"E499.MirrorCS"),sQuery(id+"F12.wireOp",EDGE,"E513.MirrorCS"),sQuery(id+"F12.wireOp",EDGE,"E514.MirrorCS"),sQuery(id+"F12.wireOp",EDGE,"E511.MirrorCS"),sQuery(id+"F12.wireOp",EDGE,"E515.MirrorCS"),sQuery(id+"F12.wireOp",EDGE,"E518.MirrorCS"),sQuery(id+"F12.wireOp",EDGE,"E519.MirrorCS")])]});
            transform(context, id + "F14", {"entities" : qUnion([Q0]), "transformType" : TransformType.TRANSLATION_3D, "dx" : 0 * mm, "dy" : 60.32 * mm, "dz" : 0 * mm, "makeCopy" : false});
        }
    });
